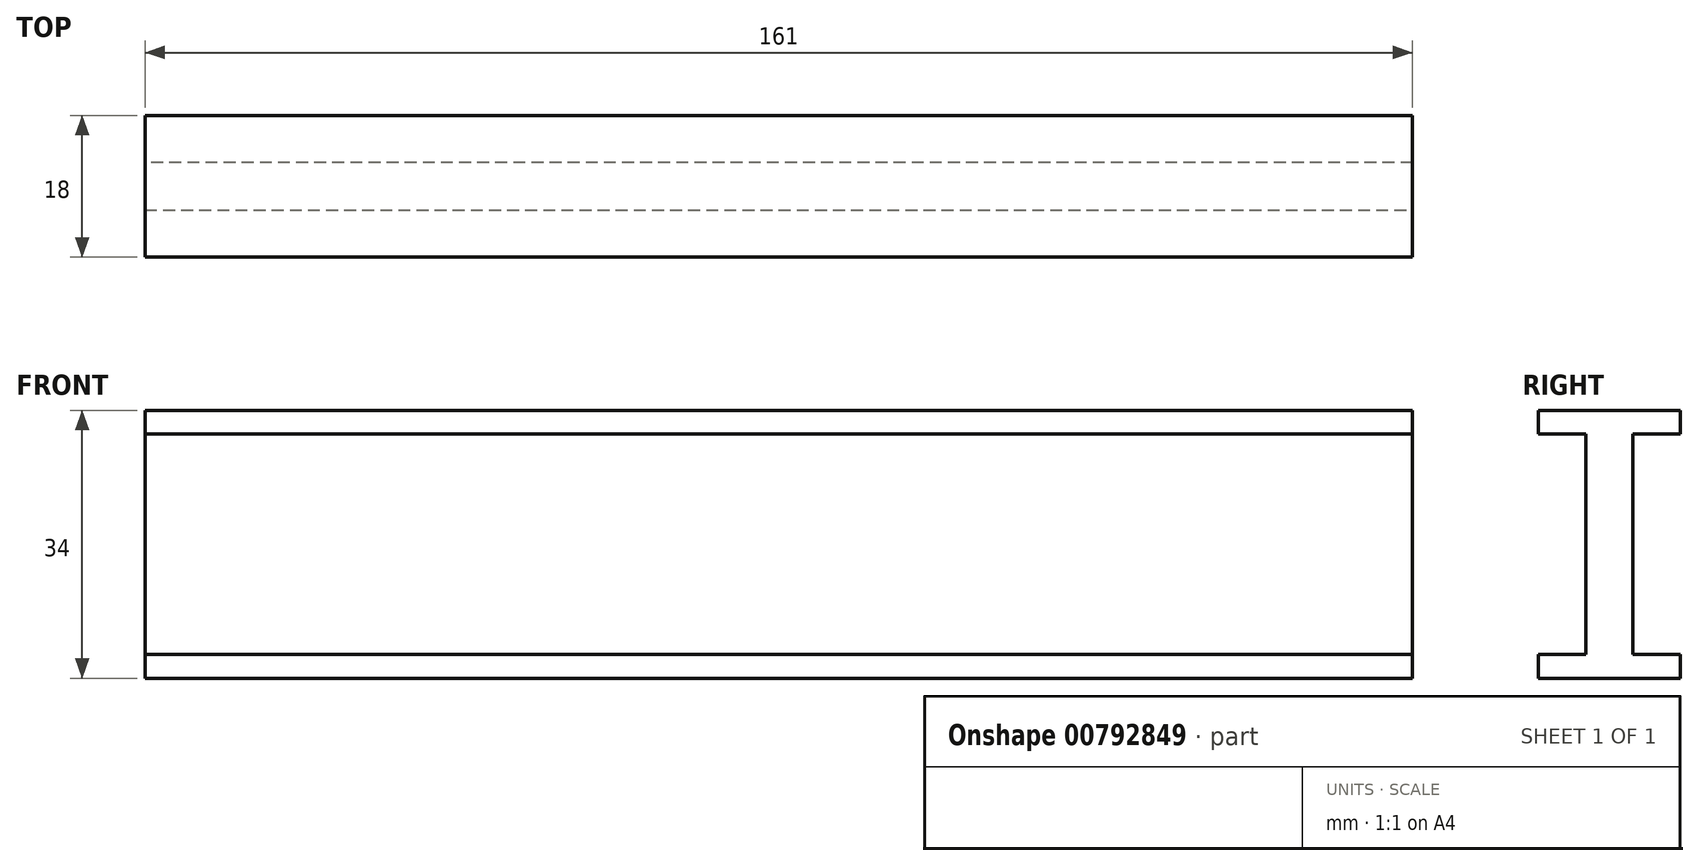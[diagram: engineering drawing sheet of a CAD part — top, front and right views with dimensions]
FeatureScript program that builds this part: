
annotation { "Feature Type Name" : "Feature", "Feature Type Description" : "" }
export const myFeature = defineFeature(function(context is Context, id is Id, definition is map)
    precondition{}
    {
        {
            var Q0;
            Q0=qCreatedBy(makeId("Front.planeOp"),FACE);
            var sketch = newSketch(context, id + "F0", { "sketchPlane" : qUnion([Q0])});
            skLineSegment(sketch, "E0.bottom", {"start": v(161, -17) * mm, "end": v(-161, -17) * mm});
            skLineSegment(sketch, "E0.top", {"start": v(161, 17) * mm, "end": v(-161, 17) * mm});
            skLineSegment(sketch, "E0.left", {"start": v(161, -17) * mm, "end": v(161, 17) * mm});
            skLineSegment(sketch, "E0.right", {"start": v(-161, -17) * mm, "end": v(-161, 17) * mm});
            skPoint(sketch, "E0.middle", {"position": v(0, 0) * mm});
            skSolve(sketch);
        }
        {
            var Q0;
            Q0 = qSketchRegion(id + "F0", true);
            extrude(context, id + "F1", {"entities" : qUnion([Q0]), "flatOperationType" : FlatOperationType.REMOVE, "depth" : 18 * mm, "offsetDistance" : 25 * mm, "domain" : OperationDomain.MODEL});
        }
        {
            var Q0;
            Q0=makeQuery(id+"F1.opExtrude","CAP_FACE",FACE,{"disambiguationData":[OSD([sQuery(id+"F0.wireOp",EDGE,"E0.bottom"),sQuery(id+"F0.wireOp",EDGE,"E0.top"),sQuery(id+"F0.wireOp",EDGE,"E0.left"),sQuery(id+"F0.wireOp",EDGE,"E0.right")])],"isStart":false});
            var sketch = newSketch(context, id + "F2", { "sketchPlane" : qUnion([Q0])});
            skLineSegment(sketch, "E1.bottom", {"start": v(-161, 14) * mm, "end": v(161, 14) * mm});
            skLineSegment(sketch, "E1.top", {"start": v(-161, -14) * mm, "end": v(161, -14) * mm});
            skLineSegment(sketch, "E1.left", {"start": v(-161, 14) * mm, "end": v(-161, -14) * mm});
            skLineSegment(sketch, "E1.right", {"start": v(161, 14) * mm, "end": v(161, -14) * mm});
            skSolve(sketch);
        }
        {
            var Q0;
            Q0 = qSketchRegion(id + "F2", true);
            extrude(context, id + "F3", {"entities" : qUnion([Q0]), "operationType" : NewBodyOperationType.REMOVE, "flatOperationType" : FlatOperationType.REMOVE, "oppositeDirection" : true, "depth" : 6 * mm, "offsetDistance" : 25 * mm, "domain" : OperationDomain.MODEL});
        }
        {
            var Q0;
            Q0=makeQuery(id+"F1.opExtrude","CAP_FACE",FACE,{"disambiguationData":[OSD([sQuery(id+"F0.wireOp",EDGE,"E0.bottom"),sQuery(id+"F0.wireOp",EDGE,"E0.top"),sQuery(id+"F0.wireOp",EDGE,"E0.left"),sQuery(id+"F0.wireOp",EDGE,"E0.right")])],"isStart":true});
            var sketch = newSketch(context, id + "F4", { "sketchPlane" : qUnion([Q0])});
            skLineSegment(sketch, "E2.bottom", {"start": v(-161, 14) * mm, "end": v(161, 14) * mm});
            skLineSegment(sketch, "E2.top", {"start": v(-161, -14) * mm, "end": v(161, -14) * mm});
            skLineSegment(sketch, "E2.left", {"start": v(-161, 14) * mm, "end": v(-161, -14) * mm});
            skLineSegment(sketch, "E2.right", {"start": v(161, 14) * mm, "end": v(161, -14) * mm});
            skSolve(sketch);
        }
        {
            var Q0;
            Q0 = qSketchRegion(id + "F4", true);
            extrude(context, id + "F5", {"entities" : qUnion([Q0]), "operationType" : NewBodyOperationType.REMOVE, "flatOperationType" : FlatOperationType.REMOVE, "oppositeDirection" : true, "depth" : 6 * mm, "offsetDistance" : 25 * mm, "domain" : OperationDomain.MODEL});
        }
        {
            var Q0;
            Q0=makeQuery(id+"F5.boolean.opBoolean","COPY",FACE,{"derivedFrom":makeQuery(id+"F5.opExtrude","CAP_FACE",FACE,{"disambiguationData":[OSD([sQuery(id+"F4.wireOp",EDGE,"E2.bottom"),sQuery(id+"F4.wireOp",EDGE,"E2.top"),sQuery(id+"F4.wireOp",EDGE,"E2.left"),sQuery(id+"F4.wireOp",EDGE,"E2.right")])],"isStart":false})});
            var sketch = newSketch(context, id + "F6", { "sketchPlane" : qUnion([Q0])});
            skLineSegment(sketch, "E3", {"start": v(0, 32.17) * mm, "end": v(161, 30.9) * mm});
            skLineSegment(sketch, "E4", {"start": v(0, -28.4) * mm, "end": v(161, -28.4) * mm});
            skLineSegment(sketch, "E5.MirrorCS", {"start": v(-161, -28.4) * mm, "end": v(-161, 30.9) * mm});
            skLineSegment(sketch, "E6", {"start": v(0, 45.25) * mm, "end": v(0, -39.27) * mm});
            skLineSegment(sketch, "E7", {"start": v(0, -28.4) * mm, "end": v(-161, -28.4) * mm});
            skLineSegment(sketch, "E8", {"start": v(0, 32.17) * mm, "end": v(-161, 30.9) * mm});
            skSolve(sketch);
        }
        {
            var Q0;
            Q0 = qSketchRegion(id + "F6", true);
            extrude(context, id + "F7", {"entities" : qUnion([Q0]), "operationType" : NewBodyOperationType.REMOVE, "oppositeDirection" : true, "depth" : 25 * mm, "offsetDistance" : 25 * mm, "hasSecondDirection" : true, "secondDirectionOppositeDirection" : false, "secondDirectionDepth" : 25 * mm});
        }
    });
